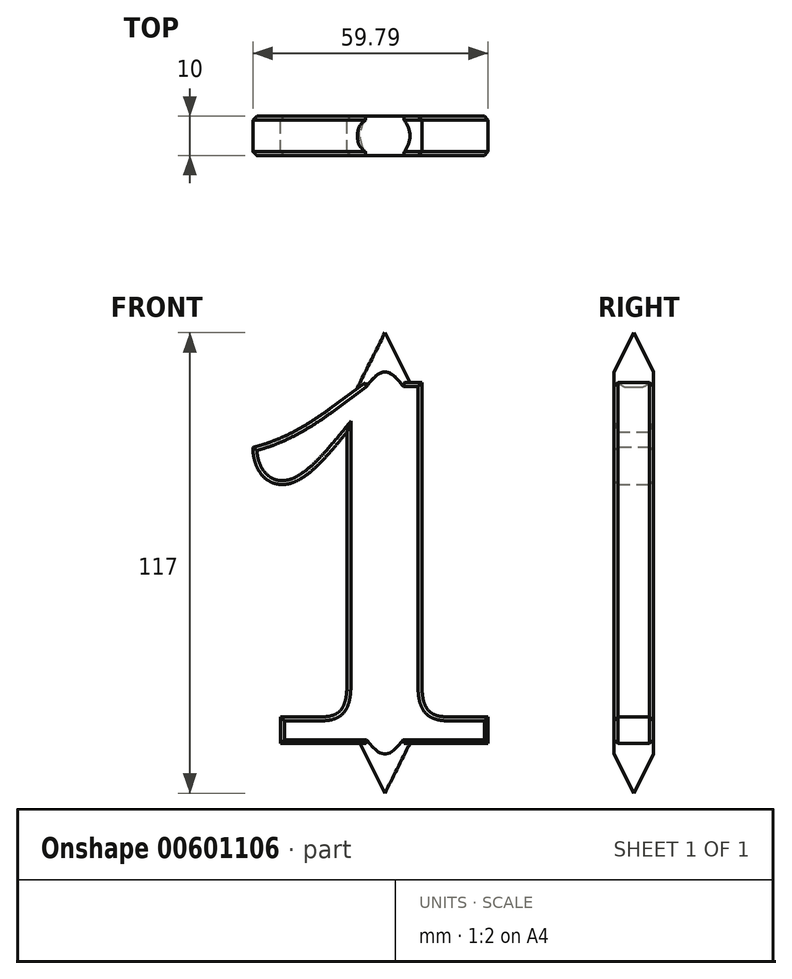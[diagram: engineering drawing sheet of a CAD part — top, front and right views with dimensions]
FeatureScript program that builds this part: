
annotation { "Feature Type Name" : "Feature", "Feature Type Description" : "" }
export const myFeature = defineFeature(function(context is Context, id is Id, definition is map)
    precondition{}
    {
        {
            var Q0;
            Q0=qCreatedBy(makeId("Front.planeOp"),FACE);
            var sketch = newSketch(context, id + "F0", { "sketchPlane" : qUnion([Q0])});
            skLineSegment(sketch, "E0", {"start": v(0, 108.8) * mm, "end": v(0, -162.25) * mm, "construction": true});
            skPoint(sketch, "E1", {"position": v(0, 0) * mm});
            skCircle(sketch, "E2", {"center": v(0, 0) * mm, "radius": 55 * mm});
            skCircle(sketch, "E3", {"center": v(0, 0) * mm, "radius": 60 * mm});
            skCircle(sketch, "E4", {"center": v(0, 0) * mm, "radius": 65 * mm});
            skArc(sketch, "E5", {"start": v(-32.84, -61.82) * mm, "mid": v(0, -70) * mm, "end": v(32.84, -61.82) * mm});
            skLineSegment(sketch, "E6", {"start": v(0, 58.5) * mm, "end": v(-3, 54.92) * mm});
            skLineSegment(sketch, "E7.MirrorCS", {"start": v(0, 58.5) * mm, "end": v(3, 54.92) * mm});
            skLineSegment(sketch, "E8.MirrorCS", {"start": v(0, -58.5) * mm, "end": v(3, -54.92) * mm});
            skLineSegment(sketch, "E9.MirrorCS", {"start": v(0, -58.5) * mm, "end": v(-3, -54.92) * mm});
            skLineSegment(sketch, "E10", {"start": v(-68.5, 0) * mm, "end": v(-64.93, 3) * mm});
            skLineSegment(sketch, "E11", {"start": v(-87.59, 0) * mm, "end": v(84.79, 0) * mm, "construction": true});
            skLineSegment(sketch, "E12", {"start": v(-68.5, 0) * mm, "end": v(-59.87, 4) * mm});
            skLineSegment(sketch, "E13.MirrorCS", {"start": v(-68.5, 0) * mm, "end": v(-64.93, -3) * mm});
            skLineSegment(sketch, "E14.MirrorCS", {"start": v(-68.5, 0) * mm, "end": v(-59.87, -4) * mm});
            skLineSegment(sketch, "E15.MirrorCS", {"start": v(68.5, 0) * mm, "end": v(59.87, -4) * mm});
            skLineSegment(sketch, "E16.MirrorCS", {"start": v(68.5, 0) * mm, "end": v(64.93, -3) * mm});
            skLineSegment(sketch, "E17.MirrorCS", {"start": v(68.5, 0) * mm, "end": v(64.93, 3) * mm});
            skLineSegment(sketch, "E18.MirrorCS", {"start": v(68.5, 0) * mm, "end": v(59.87, 4) * mm});
            skArc(sketch, "E19", {"start": v(-20.47, -232.01) * mm, "mid": v(-7.18, -135.51) * mm, "end": v(-50.64, -48.33) * mm});
            skArc(sketch, "E20", {"start": v(-66.54, -290.79) * mm, "mid": v(-5.35, -173.05) * mm, "end": v(-50.64, -48.33) * mm});
            skLineSegment(sketch, "E21", {"start": v(-70, 0) * mm, "end": v(-70, -493.69) * mm, "construction": true});
            skLineSegment(sketch, "E22", {"start": v(-70, -299.76) * mm, "end": v(0, -299.76) * mm});
            skLineSegment(sketch, "E23", {"start": v(-70, -299.76) * mm, "end": v(-66.54, -290.79) * mm});
            skArc(sketch, "E24.trimOffspring", {"start": v(-70, -299.73) * mm, "mid": v(-2.04, -188.49) * mm, "end": v(-32.84, -61.82) * mm});
            skLineSegment(sketch, "E25.trimOffspring", {"start": v(0, -299.76) * mm, "end": v(0, -400) * mm, "construction": true});
            skLineSegment(sketch, "E26.MirrorCS", {"start": v(70, -299.76) * mm, "end": v(66.54, -290.79) * mm});
            skLineSegment(sketch, "E27.MirrorCS", {"start": v(70, -299.76) * mm, "end": v(0, -299.76) * mm});
            skArc(sketch, "E28.MirrorCS", {"start": v(70, -299.73) * mm, "mid": v(2.04, -188.49) * mm, "end": v(32.84, -61.82) * mm});
            skArc(sketch, "E29.MirrorCS", {"start": v(66.54, -290.79) * mm, "mid": v(5.35, -173.05) * mm, "end": v(50.64, -48.33) * mm});
            skArc(sketch, "E30.trimOffspring", {"start": v(50.64, -48.33) * mm, "mid": v(0, 70) * mm, "end": v(-50.64, -48.33) * mm});
            skLineSegment(sketch, "E31.bottom", {"start": v(-70, -299.73) * mm, "end": v(70, -299.73) * mm});
            skLineSegment(sketch, "E31.top", {"start": v(-70, -304.73) * mm, "end": v(70, -304.73) * mm});
            skLineSegment(sketch, "E31.left", {"start": v(-70, -299.73) * mm, "end": v(-70, -304.73) * mm});
            skLineSegment(sketch, "E31.right", {"start": v(70, -299.73) * mm, "end": v(70, -304.73) * mm});
            skLineSegment(sketch, "E32", {"start": v(-59.87, 0) * mm, "end": v(-59.87, -4) * mm});
            skLineSegment(sketch, "E33", {"start": v(59.87, 4) * mm, "end": v(59.87, 0) * mm});
            skLineSegment(sketch, "E34", {"start": v(-59.87, 0) * mm, "end": v(-68.5, 0) * mm});
            skLineSegment(sketch, "E35", {"start": v(-53.44, -232.25) * mm, "end": v(49.45, -232.25) * mm, "construction": true});
            skLineSegment(sketch, "E36", {"start": v(0, -299.76) * mm, "end": v(0, -162.25) * mm, "construction": true});
            skLineSegment(sketch, "E37", {"start": v(0, -232.25) * mm, "end": v(-5, -232.25) * mm});
            skLineSegment(sketch, "E38", {"start": v(-5, -222.25) * mm, "end": v(-5, -232.25) * mm});
            skLineSegment(sketch, "E39", {"start": v(-5, -222.25) * mm, "end": v(-16.3, -222.25) * mm});
            skLineSegment(sketch, "E40.MirrorCS", {"start": v(5, -222.25) * mm, "end": v(5, -232.25) * mm});
            skLineSegment(sketch, "E41.MirrorCS", {"start": v(5, -222.25) * mm, "end": v(16.3, -222.25) * mm});
            skLineSegment(sketch, "E42", {"start": v(-5, -232.25) * mm, "end": v(5, -232.25) * mm});
            skLineSegment(sketch, "E43", {"start": v(-64.93, -3) * mm, "end": v(-64.93, 0) * mm});
            skLineSegment(sketch, "E44", {"start": v(-64.93, 0) * mm, "end": v(-68.5, 0) * mm});
            skLineSegment(sketch, "E45", {"start": v(64.93, -3) * mm, "end": v(64.93, 0) * mm});
            skLineSegment(sketch, "E46", {"start": v(64.93, 0) * mm, "end": v(68.5, 0) * mm});
            skLineSegment(sketch, "E47", {"start": v(-70, -299.73) * mm, "end": v(-70, -179.73) * mm});
            skLineSegment(sketch, "E48", {"start": v(-70, -179.73) * mm, "end": v(0, -179.73) * mm});
            skArc(sketch, "E49", {"start": v(0, -232.65) * mm, "mid": v(-16.4, -263.54) * mm, "end": v(-38.33, -290.78) * mm});
            skArc(sketch, "E50.MirrorCS", {"start": v(0, -232.65) * mm, "mid": v(16.4, -263.54) * mm, "end": v(38.33, -290.78) * mm});
            skLineSegment(sketch, "E51", {"start": v(-38.33, -290.78) * mm, "end": v(38.33, -290.78) * mm});
            skSolve(sketch);
        }
        {
            var Q0;
            Q0=qCreatedBy(makeId("Front.planeOp"),FACE);
            var sketch = newSketch(context, id + "F1", { "sketchPlane" : qUnion([Q0])});
            skText(sketch, "E52", { "text": "1", "fontName": "NotoSerif-Bold.ttf"});
            const initialGuessF1  = {"E52": [-0.03892, -0.0434, 1, 0, 0.09202]};
            skSetInitialGuess(sketch, initialGuessF1);
            skSolve(sketch);
        }
        {
            var Q0;
            Q0=qCreatedBy(makeId("Front.planeOp"),FACE);
            var sketch = newSketch(context, id + "F2", { "sketchPlane" : qUnion([Q0])});
            skPoint(sketch, "E53.0", {"position": v(0, -58.5) * mm});
            skPoint(sketch, "E54.0", {"position": v(0, 58.5) * mm});
            skLineSegment(sketch, "E55", {"start": v(0, 58.5) * mm, "end": v(-6.97, 44.58) * mm});
            skLineSegment(sketch, "E56", {"start": v(0, 44.58) * mm, "end": v(0, 58.5) * mm});
            skLineSegment(sketch, "E57", {"start": v(0, -58.5) * mm, "end": v(-6.46, -45.6) * mm});
            skLineSegment(sketch, "E58", {"start": v(-6.46, -45.6) * mm, "end": v(-8.12, -42.3) * mm});
            skLineSegment(sketch, "E59", {"start": v(0, -58.5) * mm, "end": v(0, -42.3) * mm});
            skLineSegment(sketch, "E60", {"start": v(0, 44.58) * mm, "end": v(-4.93, 44.58) * mm});
            skLineSegment(sketch, "E61", {"start": v(0, -42.3) * mm, "end": v(-7.6, -42.3) * mm});
            skPoint(sketch, "E62.end.orphan", {"position": v(-8, 42.54) * mm});
            skPoint(sketch, "E63.orphan", {"position": v(0, 42.54) * mm});
            skPoint(sketch, "E64.orphan", {"position": v(0, -39.54) * mm});
            skLineSegment(sketch, "E65", {"start": v(-6.97, 44.58) * mm, "end": v(-4.93, 44.58) * mm});
            skLineSegment(sketch, "E66", {"start": v(-8.12, -42.3) * mm, "end": v(-7.6, -42.3) * mm});
            skPoint(sketch, "E67.end.orphan", {"position": v(-7.6, -42.8) * mm});
            skPoint(sketch, "E67.start.orphan", {"position": v(-7.6, -43.31) * mm});
            skSolve(sketch);
        }
        {
            var Q0;
            Q0 = qSketchRegion(id + "F1", true);
            extrude(context, id + "F3", {"entities" : qUnion([Q0]), "endBound" : BoundingType.SYMMETRIC, "depth" : 10 * mm, "offsetDistance" : 25 * mm});
        }
        {
            var Q0;
            Q0=makeQuery(id+"F3.opExtrude","SWEPT_BODY",BODY,{"disambiguationData":[OSD([sQuery(id+"F1.wireOp",EDGE,"E52.sketch_text.stroke-0"),sQuery(id+"F1.wireOp",EDGE,"E52.sketch_text.stroke-1"),sQuery(id+"F1.wireOp",EDGE,"E52.sketch_text.stroke-2"),sQuery(id+"F1.wireOp",EDGE,"E52.sketch_text.stroke-3"),sQuery(id+"F1.wireOp",EDGE,"E52.sketch_text.stroke-4"),sQuery(id+"F1.wireOp",EDGE,"E52.sketch_text.stroke-5"),sQuery(id+"F1.wireOp",EDGE,"E52.sketch_text.stroke-6"),sQuery(id+"F1.wireOp",EDGE,"E52.sketch_text.stroke-7"),sQuery(id+"F1.wireOp",EDGE,"E52.sketch_text.stroke-8"),sQuery(id+"F1.wireOp",EDGE,"E52.sketch_text.stroke-9"),sQuery(id+"F1.wireOp",EDGE,"E52.sketch_text.stroke-10"),sQuery(id+"F1.wireOp",EDGE,"E52.sketch_text.stroke-11"),sQuery(id+"F1.wireOp",EDGE,"E52.sketch_text.stroke-12"),sQuery(id+"F1.wireOp",EDGE,"E52.sketch_text.stroke-13"),sQuery(id+"F1.wireOp",EDGE,"E52.sketch_text.stroke-14"),sQuery(id+"F1.wireOp",EDGE,"E52.sketch_text.stroke-15"),sQuery(id+"F1.wireOp",EDGE,"E52.sketch_text.stroke-16"),sQuery(id+"F1.wireOp",EDGE,"E52.sketch_text.stroke-17"),sQuery(id+"F1.wireOp",EDGE,"E52.sketch_text.stroke-18"),sQuery(id+"F1.wireOp",EDGE,"E52.sketch_text.stroke-19"),sQuery(id+"F1.wireOp",EDGE,"E52.sketch_text.stroke-20"),sQuery(id+"F1.wireOp",EDGE,"E52.sketch_text.stroke-21"),sQuery(id+"F1.wireOp",EDGE,"E52.sketch_text.stroke-22"),sQuery(id+"F1.wireOp",EDGE,"E52.sketch_text.stroke-23"),sQuery(id+"F1.wireOp",EDGE,"E52.sketch_text.stroke-24"),sQuery(id+"F1.wireOp",EDGE,"E52.sketch_text.stroke-25"),sQuery(id+"F1.wireOp",EDGE,"E52.sketch_text.stroke-26"),sQuery(id+"F1.wireOp",EDGE,"E52.sketch_text.stroke-27"),sQuery(id+"F1.wireOp",EDGE,"E52.sketch_text.stroke-28")])]});
            transform(context, id + "F4", {"entities" : qUnion([Q0]), "transformType" : TransformType.TRANSLATION_3D, "dx" : 0 * mm, "dy" : 0 * mm, "dz" : -2.5 * mm, "makeCopy" : false});
        }
        {
            var Q0;
            Q0=makeQuery(id+"F3.opExtrude","CAP_FACE",FACE,{"disambiguationData":[OSD([sQuery(id+"F1.wireOp",EDGE,"E52.sketch_text.stroke-0"),sQuery(id+"F1.wireOp",EDGE,"E52.sketch_text.stroke-1"),sQuery(id+"F1.wireOp",EDGE,"E52.sketch_text.stroke-2"),sQuery(id+"F1.wireOp",EDGE,"E52.sketch_text.stroke-3"),sQuery(id+"F1.wireOp",EDGE,"E52.sketch_text.stroke-4"),sQuery(id+"F1.wireOp",EDGE,"E52.sketch_text.stroke-5"),sQuery(id+"F1.wireOp",EDGE,"E52.sketch_text.stroke-6"),sQuery(id+"F1.wireOp",EDGE,"E52.sketch_text.stroke-7"),sQuery(id+"F1.wireOp",EDGE,"E52.sketch_text.stroke-8"),sQuery(id+"F1.wireOp",EDGE,"E52.sketch_text.stroke-9"),sQuery(id+"F1.wireOp",EDGE,"E52.sketch_text.stroke-10"),sQuery(id+"F1.wireOp",EDGE,"E52.sketch_text.stroke-11"),sQuery(id+"F1.wireOp",EDGE,"E52.sketch_text.stroke-12"),sQuery(id+"F1.wireOp",EDGE,"E52.sketch_text.stroke-13"),sQuery(id+"F1.wireOp",EDGE,"E52.sketch_text.stroke-14"),sQuery(id+"F1.wireOp",EDGE,"E52.sketch_text.stroke-15"),sQuery(id+"F1.wireOp",EDGE,"E52.sketch_text.stroke-16"),sQuery(id+"F1.wireOp",EDGE,"E52.sketch_text.stroke-17"),sQuery(id+"F1.wireOp",EDGE,"E52.sketch_text.stroke-18"),sQuery(id+"F1.wireOp",EDGE,"E52.sketch_text.stroke-19"),sQuery(id+"F1.wireOp",EDGE,"E52.sketch_text.stroke-20"),sQuery(id+"F1.wireOp",EDGE,"E52.sketch_text.stroke-21"),sQuery(id+"F1.wireOp",EDGE,"E52.sketch_text.stroke-22"),sQuery(id+"F1.wireOp",EDGE,"E52.sketch_text.stroke-23"),sQuery(id+"F1.wireOp",EDGE,"E52.sketch_text.stroke-24"),sQuery(id+"F1.wireOp",EDGE,"E52.sketch_text.stroke-25"),sQuery(id+"F1.wireOp",EDGE,"E52.sketch_text.stroke-26"),sQuery(id+"F1.wireOp",EDGE,"E52.sketch_text.stroke-27"),sQuery(id+"F1.wireOp",EDGE,"E52.sketch_text.stroke-28")])],"isStart":false});
            var Q1;
            Q1=makeQuery(id+"F3.opExtrude","CAP_FACE",FACE,{"disambiguationData":[OSD([sQuery(id+"F1.wireOp",EDGE,"E52.sketch_text.stroke-0"),sQuery(id+"F1.wireOp",EDGE,"E52.sketch_text.stroke-1"),sQuery(id+"F1.wireOp",EDGE,"E52.sketch_text.stroke-2"),sQuery(id+"F1.wireOp",EDGE,"E52.sketch_text.stroke-3"),sQuery(id+"F1.wireOp",EDGE,"E52.sketch_text.stroke-4"),sQuery(id+"F1.wireOp",EDGE,"E52.sketch_text.stroke-5"),sQuery(id+"F1.wireOp",EDGE,"E52.sketch_text.stroke-6"),sQuery(id+"F1.wireOp",EDGE,"E52.sketch_text.stroke-7"),sQuery(id+"F1.wireOp",EDGE,"E52.sketch_text.stroke-8"),sQuery(id+"F1.wireOp",EDGE,"E52.sketch_text.stroke-9"),sQuery(id+"F1.wireOp",EDGE,"E52.sketch_text.stroke-10"),sQuery(id+"F1.wireOp",EDGE,"E52.sketch_text.stroke-11"),sQuery(id+"F1.wireOp",EDGE,"E52.sketch_text.stroke-12"),sQuery(id+"F1.wireOp",EDGE,"E52.sketch_text.stroke-13"),sQuery(id+"F1.wireOp",EDGE,"E52.sketch_text.stroke-14"),sQuery(id+"F1.wireOp",EDGE,"E52.sketch_text.stroke-15"),sQuery(id+"F1.wireOp",EDGE,"E52.sketch_text.stroke-16"),sQuery(id+"F1.wireOp",EDGE,"E52.sketch_text.stroke-17"),sQuery(id+"F1.wireOp",EDGE,"E52.sketch_text.stroke-18"),sQuery(id+"F1.wireOp",EDGE,"E52.sketch_text.stroke-19"),sQuery(id+"F1.wireOp",EDGE,"E52.sketch_text.stroke-20"),sQuery(id+"F1.wireOp",EDGE,"E52.sketch_text.stroke-21"),sQuery(id+"F1.wireOp",EDGE,"E52.sketch_text.stroke-22"),sQuery(id+"F1.wireOp",EDGE,"E52.sketch_text.stroke-23"),sQuery(id+"F1.wireOp",EDGE,"E52.sketch_text.stroke-24"),sQuery(id+"F1.wireOp",EDGE,"E52.sketch_text.stroke-25"),sQuery(id+"F1.wireOp",EDGE,"E52.sketch_text.stroke-26"),sQuery(id+"F1.wireOp",EDGE,"E52.sketch_text.stroke-27"),sQuery(id+"F1.wireOp",EDGE,"E52.sketch_text.stroke-28")])],"isStart":true});
            chamfer(context, id + "F5", {"entities" : qUnion([Q0, Q1]), "width" : 1 * mm, "tangentPropagation" : true});
        }
        {
            var Q0;
            Q0=makeQuery(id+"F2.imprint","IMPRINT",FACE,{"disambiguationData":[TD([[makeQuery(id+"F2.imprint","IMPRINT",EDGE,{"derivedFrom":sQuery(id+"F2.wireOp",EDGE,"E55")}),1.0]])]});
            var Q1;
            Q1=makeQuery(id+"F2.imprint","IMPRINT",FACE,{"disambiguationData":[TD([[makeQuery(id+"F2.imprint","IMPRINT",EDGE,{"derivedFrom":sQuery(id+"F2.wireOp",EDGE,"E57")}),-1.0]])]});
            var Q2;
            Q2=sQuery(id+"F0.wireOp",EDGE,"E0");
            revolve(context, id + "F6", {"operationType" : NewBodyOperationType.ADD, "entities" : qUnion([Q0, Q1]), "axis" : qUnion([Q2]), "revolveType" : RevolveType.FULL});
        }
        {
            var Q0;
            Q0=makeQuery(id+"F3.opExtrude","CAP_FACE",FACE,{"disambiguationData":[OSD([sQuery(id+"F1.wireOp",EDGE,"E52.sketch_text.stroke-0"),sQuery(id+"F1.wireOp",EDGE,"E52.sketch_text.stroke-1"),sQuery(id+"F1.wireOp",EDGE,"E52.sketch_text.stroke-2"),sQuery(id+"F1.wireOp",EDGE,"E52.sketch_text.stroke-3"),sQuery(id+"F1.wireOp",EDGE,"E52.sketch_text.stroke-4"),sQuery(id+"F1.wireOp",EDGE,"E52.sketch_text.stroke-5"),sQuery(id+"F1.wireOp",EDGE,"E52.sketch_text.stroke-6"),sQuery(id+"F1.wireOp",EDGE,"E52.sketch_text.stroke-7"),sQuery(id+"F1.wireOp",EDGE,"E52.sketch_text.stroke-8"),sQuery(id+"F1.wireOp",EDGE,"E52.sketch_text.stroke-9"),sQuery(id+"F1.wireOp",EDGE,"E52.sketch_text.stroke-10"),sQuery(id+"F1.wireOp",EDGE,"E52.sketch_text.stroke-11"),sQuery(id+"F1.wireOp",EDGE,"E52.sketch_text.stroke-12"),sQuery(id+"F1.wireOp",EDGE,"E52.sketch_text.stroke-13"),sQuery(id+"F1.wireOp",EDGE,"E52.sketch_text.stroke-14"),sQuery(id+"F1.wireOp",EDGE,"E52.sketch_text.stroke-15"),sQuery(id+"F1.wireOp",EDGE,"E52.sketch_text.stroke-16"),sQuery(id+"F1.wireOp",EDGE,"E52.sketch_text.stroke-17"),sQuery(id+"F1.wireOp",EDGE,"E52.sketch_text.stroke-18"),sQuery(id+"F1.wireOp",EDGE,"E52.sketch_text.stroke-19"),sQuery(id+"F1.wireOp",EDGE,"E52.sketch_text.stroke-20"),sQuery(id+"F1.wireOp",EDGE,"E52.sketch_text.stroke-21"),sQuery(id+"F1.wireOp",EDGE,"E52.sketch_text.stroke-22"),sQuery(id+"F1.wireOp",EDGE,"E52.sketch_text.stroke-23"),sQuery(id+"F1.wireOp",EDGE,"E52.sketch_text.stroke-24"),sQuery(id+"F1.wireOp",EDGE,"E52.sketch_text.stroke-25"),sQuery(id+"F1.wireOp",EDGE,"E52.sketch_text.stroke-26"),sQuery(id+"F1.wireOp",EDGE,"E52.sketch_text.stroke-27"),sQuery(id+"F1.wireOp",EDGE,"E52.sketch_text.stroke-28")])],"isStart":false});
            var sketch = newSketch(context, id + "F7", { "sketchPlane" : qUnion([Q0])});
            skPoint(sketch, "E68.0", {"position": v(-38.92, 48.62) * mm});
            skPoint(sketch, "E69.0", {"position": v(34.52, -43.4) * mm});
            skLineSegment(sketch, "E70.left", {"start": v(-38.92, 48.62) * mm, "end": v(-38.92, -43.4) * mm});
            skLineSegment(sketch, "E70.right", {"start": v(34.52, 48.62) * mm, "end": v(34.52, -43.4) * mm});
            skLineSegment(sketch, "E71.top", {"start": v(-38.92, -58.8) * mm, "end": v(34.52, -58.8) * mm});
            skLineSegment(sketch, "E71.left", {"start": v(-38.92, -43.4) * mm, "end": v(-38.92, -58.8) * mm});
            skLineSegment(sketch, "E71.right", {"start": v(34.52, -43.4) * mm, "end": v(34.52, -58.8) * mm});
            skLineSegment(sketch, "E72.top", {"start": v(-38.92, 62.38) * mm, "end": v(34.52, 62.38) * mm});
            skLineSegment(sketch, "E72.left", {"start": v(-38.92, 48.62) * mm, "end": v(-38.92, 62.38) * mm});
            skLineSegment(sketch, "E72.right", {"start": v(34.52, 48.62) * mm, "end": v(34.52, 62.38) * mm});
            skSolve(sketch);
        }
        {
            var Q0;
            Q0=makeQuery(id+"F7.imprint","IMPRINT",FACE,{"disambiguationData":[TD([[makeQuery(id+"F7.imprint","IMPRINT",EDGE,{"derivedFrom":sQuery(id+"F7.wireOp",EDGE,"E70.bottom")}),-1.0]])]});
            var Q1;
            {var subQ0=sQuery(id+"F1.wireOp",EDGE,"E52.sketch_text.stroke-28");var subQ1=sQuery(id+"F1.wireOp",EDGE,"E52.sketch_text.stroke-27");var subQ2=sQuery(id+"F1.wireOp",EDGE,"E52.sketch_text.stroke-26");var subQ3=sQuery(id+"F1.wireOp",EDGE,"E52.sketch_text.stroke-25");var subQ4=sQuery(id+"F1.wireOp",EDGE,"E52.sketch_text.stroke-24");var subQ5=sQuery(id+"F1.wireOp",EDGE,"E52.sketch_text.stroke-23");var subQ6=sQuery(id+"F1.wireOp",EDGE,"E52.sketch_text.stroke-22");var subQ7=sQuery(id+"F1.wireOp",EDGE,"E52.sketch_text.stroke-21");var subQ8=sQuery(id+"F1.wireOp",EDGE,"E52.sketch_text.stroke-20");var subQ9=sQuery(id+"F1.wireOp",EDGE,"E52.sketch_text.stroke-19");var subQ10=sQuery(id+"F1.wireOp",EDGE,"E52.sketch_text.stroke-18");var subQ11=sQuery(id+"F1.wireOp",EDGE,"E52.sketch_text.stroke-17");var subQ12=sQuery(id+"F1.wireOp",EDGE,"E52.sketch_text.stroke-16");var subQ13=sQuery(id+"F1.wireOp",EDGE,"E52.sketch_text.stroke-15");var subQ14=sQuery(id+"F1.wireOp",EDGE,"E52.sketch_text.stroke-14");var subQ15=sQuery(id+"F1.wireOp",EDGE,"E52.sketch_text.stroke-13");var subQ16=sQuery(id+"F1.wireOp",EDGE,"E52.sketch_text.stroke-12");var subQ17=sQuery(id+"F1.wireOp",EDGE,"E52.sketch_text.stroke-11");var subQ18=sQuery(id+"F1.wireOp",EDGE,"E52.sketch_text.stroke-10");var subQ19=sQuery(id+"F1.wireOp",EDGE,"E52.sketch_text.stroke-9");var subQ20=sQuery(id+"F1.wireOp",EDGE,"E52.sketch_text.stroke-8");var subQ21=sQuery(id+"F1.wireOp",EDGE,"E52.sketch_text.stroke-7");var subQ22=sQuery(id+"F1.wireOp",EDGE,"E52.sketch_text.stroke-6");var subQ23=sQuery(id+"F1.wireOp",EDGE,"E52.sketch_text.stroke-5");var subQ24=sQuery(id+"F1.wireOp",EDGE,"E52.sketch_text.stroke-4");var subQ25=sQuery(id+"F1.wireOp",EDGE,"E52.sketch_text.stroke-3");var subQ26=sQuery(id+"F1.wireOp",EDGE,"E52.sketch_text.stroke-2");var subQ27=sQuery(id+"F1.wireOp",EDGE,"E52.sketch_text.stroke-1");var subQ28=sQuery(id+"F1.wireOp",EDGE,"E52.sketch_text.stroke-0");var subQ29=makeQuery(id+"F3.opExtrude","CAP_FACE",FACE,{"disambiguationData":[OSD([subQ28,subQ27,subQ26,subQ25,subQ24,subQ23,subQ22,subQ21,subQ20,subQ19,subQ18,subQ17,subQ16,subQ15,subQ14,subQ13,subQ12,subQ11,subQ10,subQ9,subQ8,subQ7,subQ6,subQ5,subQ4,subQ3,subQ2,subQ1,subQ0])],"isStart":false});var subQ32=makeQuery(id+"F3.opExtrude","CAP_EDGE",EDGE,{"disambiguationData":[OSD([subQ28])],"isStart":false});Q1=makeQuery(id+"F7.imprint","IMPRINT",FACE,{"disambiguationData":[TD([[makeQuery(id+"F7.imprint","IMPRINT",EDGE,{"derivedFrom":makeQuery(id+"F5.opChamfer","BLEND_EDGE",EDGE,{"blendedFrom":[subQ32,subQ29],"blendedInto":[subQ29]})}),1.0]])]});}
            var Q2;
            Q2=makeQuery(id+"F7.imprint","IMPRINT",FACE,{"disambiguationData":[TD([[makeQuery(id+"F7.imprint","IMPRINT",EDGE,{"derivedFrom":sQuery(id+"F7.wireOp",EDGE,"E70.left")}),1.0]])]});
            extrude(context, id + "F8", {"entities" : qUnion([Q0, Q1, Q2]), "operationType" : NewBodyOperationType.REMOVE, "depth" : 25 * mm, "offsetDistance" : 25 * mm});
        }
        {
            var Q0;
            Q0=makeQuery(id+"F3.opExtrude","CAP_FACE",FACE,{"disambiguationData":[OSD([sQuery(id+"F1.wireOp",EDGE,"E52.sketch_text.stroke-0"),sQuery(id+"F1.wireOp",EDGE,"E52.sketch_text.stroke-1"),sQuery(id+"F1.wireOp",EDGE,"E52.sketch_text.stroke-2"),sQuery(id+"F1.wireOp",EDGE,"E52.sketch_text.stroke-3"),sQuery(id+"F1.wireOp",EDGE,"E52.sketch_text.stroke-4"),sQuery(id+"F1.wireOp",EDGE,"E52.sketch_text.stroke-5"),sQuery(id+"F1.wireOp",EDGE,"E52.sketch_text.stroke-6"),sQuery(id+"F1.wireOp",EDGE,"E52.sketch_text.stroke-7"),sQuery(id+"F1.wireOp",EDGE,"E52.sketch_text.stroke-8"),sQuery(id+"F1.wireOp",EDGE,"E52.sketch_text.stroke-9"),sQuery(id+"F1.wireOp",EDGE,"E52.sketch_text.stroke-10"),sQuery(id+"F1.wireOp",EDGE,"E52.sketch_text.stroke-11"),sQuery(id+"F1.wireOp",EDGE,"E52.sketch_text.stroke-12"),sQuery(id+"F1.wireOp",EDGE,"E52.sketch_text.stroke-13"),sQuery(id+"F1.wireOp",EDGE,"E52.sketch_text.stroke-14"),sQuery(id+"F1.wireOp",EDGE,"E52.sketch_text.stroke-15"),sQuery(id+"F1.wireOp",EDGE,"E52.sketch_text.stroke-16"),sQuery(id+"F1.wireOp",EDGE,"E52.sketch_text.stroke-17"),sQuery(id+"F1.wireOp",EDGE,"E52.sketch_text.stroke-18"),sQuery(id+"F1.wireOp",EDGE,"E52.sketch_text.stroke-19"),sQuery(id+"F1.wireOp",EDGE,"E52.sketch_text.stroke-20"),sQuery(id+"F1.wireOp",EDGE,"E52.sketch_text.stroke-21"),sQuery(id+"F1.wireOp",EDGE,"E52.sketch_text.stroke-22"),sQuery(id+"F1.wireOp",EDGE,"E52.sketch_text.stroke-23"),sQuery(id+"F1.wireOp",EDGE,"E52.sketch_text.stroke-24"),sQuery(id+"F1.wireOp",EDGE,"E52.sketch_text.stroke-25"),sQuery(id+"F1.wireOp",EDGE,"E52.sketch_text.stroke-26"),sQuery(id+"F1.wireOp",EDGE,"E52.sketch_text.stroke-27"),sQuery(id+"F1.wireOp",EDGE,"E52.sketch_text.stroke-28")])],"isStart":true});
            var sketch = newSketch(context, id + "F9", { "sketchPlane" : qUnion([Q0])});
            skLineSegment(sketch, "E73.bottom", {"start": v(-37.22, 63.98) * mm, "end": v(41.68, 63.98) * mm});
            skLineSegment(sketch, "E73.top", {"start": v(-37.22, -58.42) * mm, "end": v(41.68, -58.42) * mm});
            skLineSegment(sketch, "E73.left", {"start": v(-37.22, 63.98) * mm, "end": v(-37.22, -58.42) * mm});
            skLineSegment(sketch, "E73.right", {"start": v(41.68, 63.98) * mm, "end": v(41.68, -58.42) * mm});
            skSolve(sketch);
        }
        {
            var Q0;
            Q0=makeQuery(id+"F9.imprint","IMPRINT",FACE,{"disambiguationData":[TD([[makeQuery(id+"F9.imprint","IMPRINT",EDGE,{"derivedFrom":sQuery(id+"F9.wireOp",EDGE,"E73.bottom")}),-1.0]])]});
            var Q1;
            {var subQ0=sQuery(id+"F1.wireOp",EDGE,"E52.sketch_text.stroke-28");var subQ1=sQuery(id+"F1.wireOp",EDGE,"E52.sketch_text.stroke-27");var subQ2=sQuery(id+"F1.wireOp",EDGE,"E52.sketch_text.stroke-26");var subQ3=sQuery(id+"F1.wireOp",EDGE,"E52.sketch_text.stroke-25");var subQ4=sQuery(id+"F1.wireOp",EDGE,"E52.sketch_text.stroke-24");var subQ5=sQuery(id+"F1.wireOp",EDGE,"E52.sketch_text.stroke-23");var subQ6=sQuery(id+"F1.wireOp",EDGE,"E52.sketch_text.stroke-22");var subQ7=sQuery(id+"F1.wireOp",EDGE,"E52.sketch_text.stroke-21");var subQ8=sQuery(id+"F1.wireOp",EDGE,"E52.sketch_text.stroke-20");var subQ9=sQuery(id+"F1.wireOp",EDGE,"E52.sketch_text.stroke-19");var subQ10=sQuery(id+"F1.wireOp",EDGE,"E52.sketch_text.stroke-18");var subQ11=sQuery(id+"F1.wireOp",EDGE,"E52.sketch_text.stroke-17");var subQ12=sQuery(id+"F1.wireOp",EDGE,"E52.sketch_text.stroke-16");var subQ13=sQuery(id+"F1.wireOp",EDGE,"E52.sketch_text.stroke-15");var subQ14=sQuery(id+"F1.wireOp",EDGE,"E52.sketch_text.stroke-14");var subQ15=sQuery(id+"F1.wireOp",EDGE,"E52.sketch_text.stroke-13");var subQ16=sQuery(id+"F1.wireOp",EDGE,"E52.sketch_text.stroke-12");var subQ17=sQuery(id+"F1.wireOp",EDGE,"E52.sketch_text.stroke-11");var subQ18=sQuery(id+"F1.wireOp",EDGE,"E52.sketch_text.stroke-10");var subQ19=sQuery(id+"F1.wireOp",EDGE,"E52.sketch_text.stroke-9");var subQ20=sQuery(id+"F1.wireOp",EDGE,"E52.sketch_text.stroke-8");var subQ21=sQuery(id+"F1.wireOp",EDGE,"E52.sketch_text.stroke-7");var subQ22=sQuery(id+"F1.wireOp",EDGE,"E52.sketch_text.stroke-6");var subQ23=sQuery(id+"F1.wireOp",EDGE,"E52.sketch_text.stroke-5");var subQ24=sQuery(id+"F1.wireOp",EDGE,"E52.sketch_text.stroke-4");var subQ25=sQuery(id+"F1.wireOp",EDGE,"E52.sketch_text.stroke-3");var subQ26=sQuery(id+"F1.wireOp",EDGE,"E52.sketch_text.stroke-2");var subQ27=sQuery(id+"F1.wireOp",EDGE,"E52.sketch_text.stroke-1");var subQ28=sQuery(id+"F1.wireOp",EDGE,"E52.sketch_text.stroke-0");var subQ29=makeQuery(id+"F3.opExtrude","CAP_FACE",FACE,{"disambiguationData":[OSD([subQ28,subQ27,subQ26,subQ25,subQ24,subQ23,subQ22,subQ21,subQ20,subQ19,subQ18,subQ17,subQ16,subQ15,subQ14,subQ13,subQ12,subQ11,subQ10,subQ9,subQ8,subQ7,subQ6,subQ5,subQ4,subQ3,subQ2,subQ1,subQ0])],"isStart":true});var subQ30=makeQuery(id+"F3.opExtrude","CAP_EDGE",EDGE,{"disambiguationData":[OSD([subQ28])],"isStart":true});Q1=makeQuery(id+"F9.imprint","IMPRINT",FACE,{"disambiguationData":[TD([[makeQuery(id+"F9.imprint","IMPRINT",EDGE,{"derivedFrom":makeQuery(id+"F5.opChamfer","BLEND_EDGE",EDGE,{"blendedFrom":[subQ30,subQ29],"blendedInto":[subQ29]})}),1.0]])]});}
            extrude(context, id + "F10", {"entities" : qUnion([Q0, Q1]), "operationType" : NewBodyOperationType.REMOVE, "depth" : 25 * mm, "offsetDistance" : 25 * mm});
        }
    });
